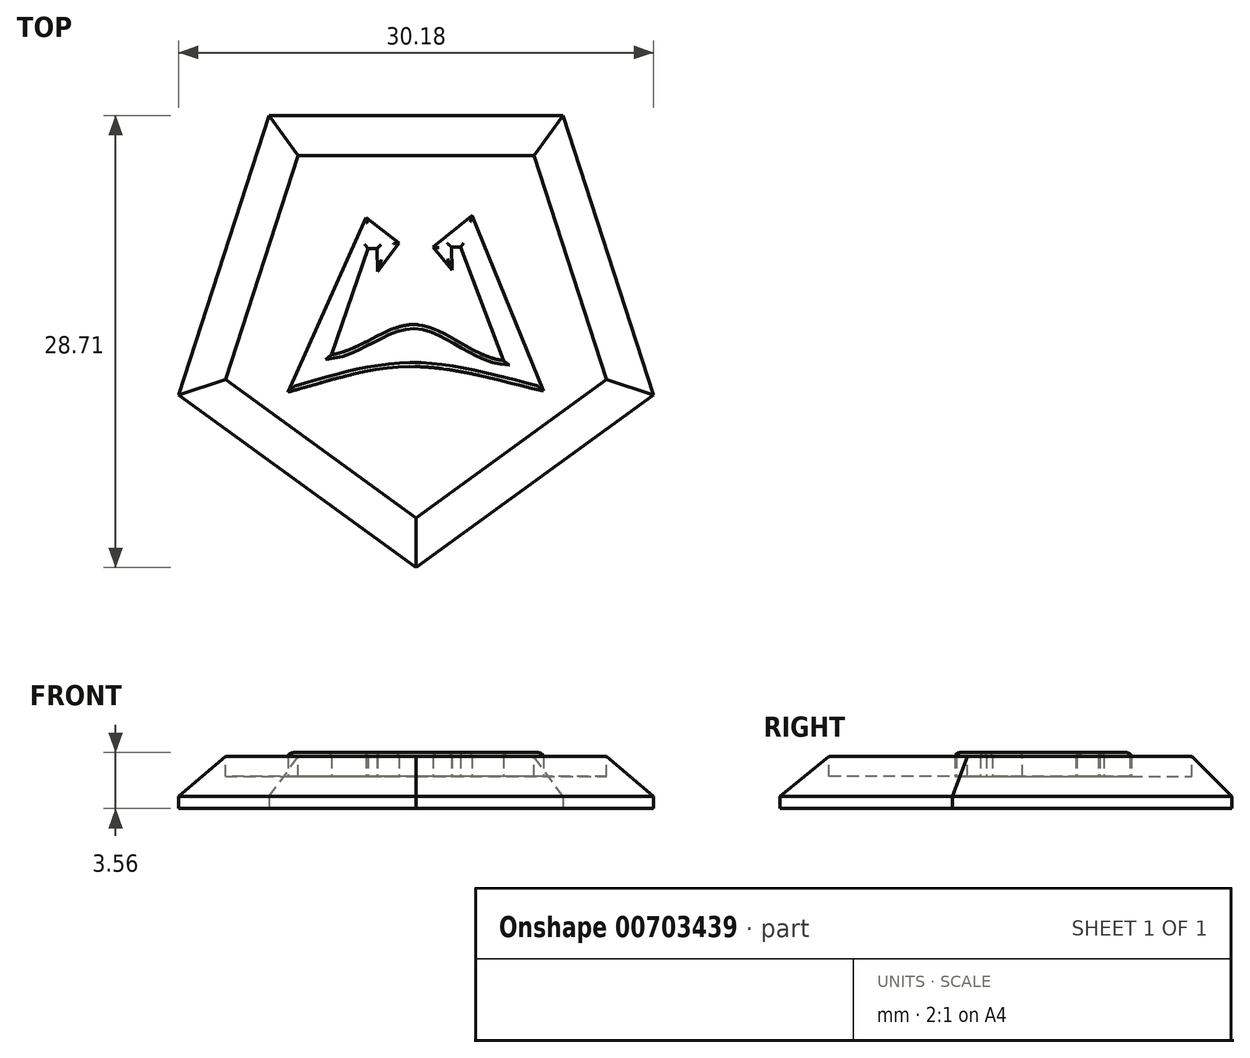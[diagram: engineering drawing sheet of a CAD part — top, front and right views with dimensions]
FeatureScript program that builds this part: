
annotation { "Feature Type Name" : "Feature", "Feature Type Description" : "" }
export const myFeature = defineFeature(function(context is Context, id is Id, definition is map)
    precondition{}
    {
        {
            var Q0;
            Q0=qCreatedBy(makeId("Top.planeOp"),FACE);
            var sketch = newSketch(context, id + "F0", { "sketchPlane" : qUnion([Q0])});
            skCircle(sketch, "E0.cCircle", {"center": v(0, 0) * mm, "radius": 12.84 * mm, "construction": true});
            skLineSegment(sketch, "E0.0", {"start": v(-9.33, 12.84) * mm, "end": v(9.33, 12.84) * mm});
            skLineSegment(sketch, "E0.1", {"start": v(9.33, 12.84) * mm, "end": v(15.09, -4.9) * mm});
            skLineSegment(sketch, "E0.2", {"start": v(15.09, -4.9) * mm, "end": v(0, -15.87) * mm});
            skLineSegment(sketch, "E0.3", {"start": v(0, -15.87) * mm, "end": v(-15.09, -4.9) * mm});
            skLineSegment(sketch, "E0.4", {"start": v(-15.09, -4.9) * mm, "end": v(-9.33, 12.84) * mm});
            skPoint(sketch, "E0.0.midPoint", {"position": v(0, 12.84) * mm});
            skSolve(sketch);
        }
        {
            var Q0;
            Q0=makeQuery(id+"F0.imprint","IMPRINT",FACE,{"disambiguationData":[TD([[makeQuery(id+"F0.imprint","IMPRINT",EDGE,{"derivedFrom":sQuery(id+"F0.wireOp",EDGE,"E0.0")}),-1.0]])]});
            extrude(context, id + "F1", {"entities" : qUnion([Q0]), "depth" : 3.3 * mm, "offsetDistance" : 25.4 * mm});
        }
        {
            var Q0;
            Q0=makeQuery(id+"F1.opExtrude","CAP_FACE",FACE,{"disambiguationData":[OSD([sQuery(id+"F0.wireOp",EDGE,"E0.0"),sQuery(id+"F0.wireOp",EDGE,"E0.1"),sQuery(id+"F0.wireOp",EDGE,"E0.2"),sQuery(id+"F0.wireOp",EDGE,"E0.3"),sQuery(id+"F0.wireOp",EDGE,"E0.4")])],"isStart":false});
            var sketch = newSketch(context, id + "F2", { "sketchPlane" : qUnion([Q0])});
            skCircle(sketch, "E1.cCircle", {"center": v(0, 0) * mm, "radius": 10.16 * mm, "construction": true});
            skPoint(sketch, "E1.cCircle.perimeterSnap0", {"position": v(0, 12.84) * mm});
            skLineSegment(sketch, "E1.0", {"start": v(-7.38, 10.16) * mm, "end": v(7.38, 10.16) * mm, "construction": true});
            skLineSegment(sketch, "E1.1", {"start": v(7.38, 10.16) * mm, "end": v(11.95, -3.88) * mm, "construction": true});
            skLineSegment(sketch, "E1.2", {"start": v(11.95, -3.88) * mm, "end": v(0, -12.56) * mm});
            skLineSegment(sketch, "E1.3", {"start": v(0, -12.56) * mm, "end": v(-11.95, -3.88) * mm});
            skLineSegment(sketch, "E1.4", {"start": v(-11.95, -3.88) * mm, "end": v(-7.38, 10.16) * mm, "construction": true});
            skPoint(sketch, "E1.0.midPoint", {"position": v(0, 10.16) * mm});
            skPoint(sketch, "E1.0.midPoint.positionSnap0", {"position": v(0, 12.84) * mm});
            skPoint(sketch, "E2.endSnap0", {"position": v(-9.67, 3.14) * mm});
            skFitSpline(sketch, "E3", {"points": [v(8.08, -4.65) * mm, v(0.01, -3.12) * mm, v(-8.15, -4.74) * mm], "startDerivative": vector(-13.47, 2.85) * mm, "endDerivative": vector(-16.78, -4.65) * mm});
            skLineSegment(sketch, "E4", {"start": v(-8.15, -4.74) * mm, "end": v(-5.43, 1.33) * mm});
            skLineSegment(sketch, "E5", {"start": v(-5.43, 1.33) * mm, "end": v(-3.19, 6.36) * mm});
            skLineSegment(sketch, "E6", {"start": v(3.54, 6.48) * mm, "end": v(1.09, 4.47) * mm});
            skLineSegment(sketch, "E7", {"start": v(1.09, 4.47) * mm, "end": v(2.27, 3.02) * mm});
            skPoint(sketch, "E7.endSnap0", {"position": v(0, 1.56) * mm});
            skLineSegment(sketch, "E8", {"start": v(2.27, 3.02) * mm, "end": v(2.25, 4.47) * mm});
            skLineSegment(sketch, "E9", {"start": v(-3.19, 6.36) * mm, "end": v(-1.1, 4.73) * mm});
            skLineSegment(sketch, "E10", {"start": v(-1.1, 4.73) * mm, "end": v(-2.44, 2.94) * mm});
            skLineSegment(sketch, "E11", {"start": v(-2.44, 2.94) * mm, "end": v(-2.47, 4.39) * mm});
            skLineSegment(sketch, "E12", {"start": v(-3.06, 4.38) * mm, "end": v(-5.37, -2.35) * mm});
            skLineSegment(sketch, "E13", {"start": v(5.54, -2.72) * mm, "end": v(2.84, 4.48) * mm});
            skFitSpline(sketch, "E14", {"points": [v(5.54, -2.72) * mm, v(-0.03, -0.44) * mm, v(-5.37, -2.35) * mm], "startDerivative": vector(-11.34, 1.14) * mm, "endDerivative": vector(-11.24, -1.53) * mm});
            skLineSegment(sketch, "E15", {"start": v(2.25, 4.47) * mm, "end": v(2.84, 4.48) * mm});
            skLineSegment(sketch, "E16", {"start": v(-2.47, 4.39) * mm, "end": v(-3.06, 4.38) * mm});
            skLineSegment(sketch, "E17", {"start": v(8.08, -4.65) * mm, "end": v(3.54, 6.48) * mm});
            skSolve(sketch);
        }
        {
            var Q0;
            Q0=qSketchRegion(id+"F2",true);
            extrude(context, id + "F3", {"entities" : qUnion([Q0]), "operationType" : NewBodyOperationType.ADD, "depth" : 0.25 * mm, "offsetDistance" : 25.4 * mm});
        }
        {
            var Q0;
            Q0=makeQuery(id+"F1.opExtrude","CAP_EDGE",EDGE,{"disambiguationData":[OSD([sQuery(id+"F0.wireOp",EDGE,"E0.2")])],"isStart":false});
            var Q1;
            Q1=makeQuery(id+"F1.opExtrude","CAP_EDGE",EDGE,{"disambiguationData":[OSD([sQuery(id+"F0.wireOp",EDGE,"E0.3")])],"isStart":false});
            var Q2;
            Q2=makeQuery(id+"F1.opExtrude","CAP_EDGE",EDGE,{"disambiguationData":[OSD([sQuery(id+"F0.wireOp",EDGE,"E0.4")])],"isStart":false});
            var Q3;
            Q3=makeQuery(id+"F1.opExtrude","CAP_EDGE",EDGE,{"disambiguationData":[OSD([sQuery(id+"F0.wireOp",EDGE,"E0.0")])],"isStart":false});
            var Q4;
            Q4=makeQuery(id+"F1.opExtrude","CAP_EDGE",EDGE,{"disambiguationData":[OSD([sQuery(id+"F0.wireOp",EDGE,"E0.1")])],"isStart":false});
            chamfer(context, id + "F4", {"entities" : qUnion([Q0, Q1, Q2, Q3, Q4]), "width" : 2.54 * mm, "tangentPropagation" : true});
        }
        {
            var Q0;
            {var subQ0=sQuery(id+"F0.wireOp",EDGE,"E0.2");var subQ1=sQuery(id+"F0.wireOp",EDGE,"E0.1");var subQ2=sQuery(id+"F0.wireOp",EDGE,"E0.3");var subQ3=sQuery(id+"F0.wireOp",EDGE,"E0.0");var subQ4=sQuery(id+"F0.wireOp",EDGE,"E0.4");Q0=makeQuery(id+"F3.boolean.opBoolean","SPLIT",FACE,{"disambiguationData":[TD([makeQuery(id+"F1.opExtrude","SWEPT_FACE",FACE,{"disambiguationData":[OSD([subQ3])]})])],"derivedFrom":makeQuery(id+"F1.opExtrude","CAP_FACE",FACE,{"disambiguationData":[OSD([subQ3,subQ1,subQ0,subQ2,subQ4])],"isStart":false})});}
            extrude(context, id + "F5", {"entities" : qUnion([Q0]), "operationType" : NewBodyOperationType.REMOVE, "oppositeDirection" : true, "depth" : 1.27 * mm, "offsetDistance" : 25.4 * mm});
        }
        {
            var Q0;
            Q0=makeQuery(id+"F3.opExtrude","CAP_FACE",FACE,{"disambiguationData":[OSD([sQuery(id+"F2.wireOp",EDGE,"E3"),sQuery(id+"F2.wireOp",EDGE,"E4"),sQuery(id+"F2.wireOp",EDGE,"E5"),sQuery(id+"F2.wireOp",EDGE,"E6"),sQuery(id+"F2.wireOp",EDGE,"E7"),sQuery(id+"F2.wireOp",EDGE,"E8"),sQuery(id+"F2.wireOp",EDGE,"E9"),sQuery(id+"F2.wireOp",EDGE,"E10"),sQuery(id+"F2.wireOp",EDGE,"E11"),sQuery(id+"F2.wireOp",EDGE,"E12"),sQuery(id+"F2.wireOp",EDGE,"E13"),sQuery(id+"F2.wireOp",EDGE,"E14"),sQuery(id+"F2.wireOp",EDGE,"E15"),sQuery(id+"F2.wireOp",EDGE,"E16"),sQuery(id+"F2.wireOp",EDGE,"E17")])],"isStart":false});
            fillet(context, id + "F6", {"entities" : qUnion([Q0]), "radius" : 0.25 * mm, "tangentPropagation" : true, "allowEdgeOverflow" : false});
        }
    });
